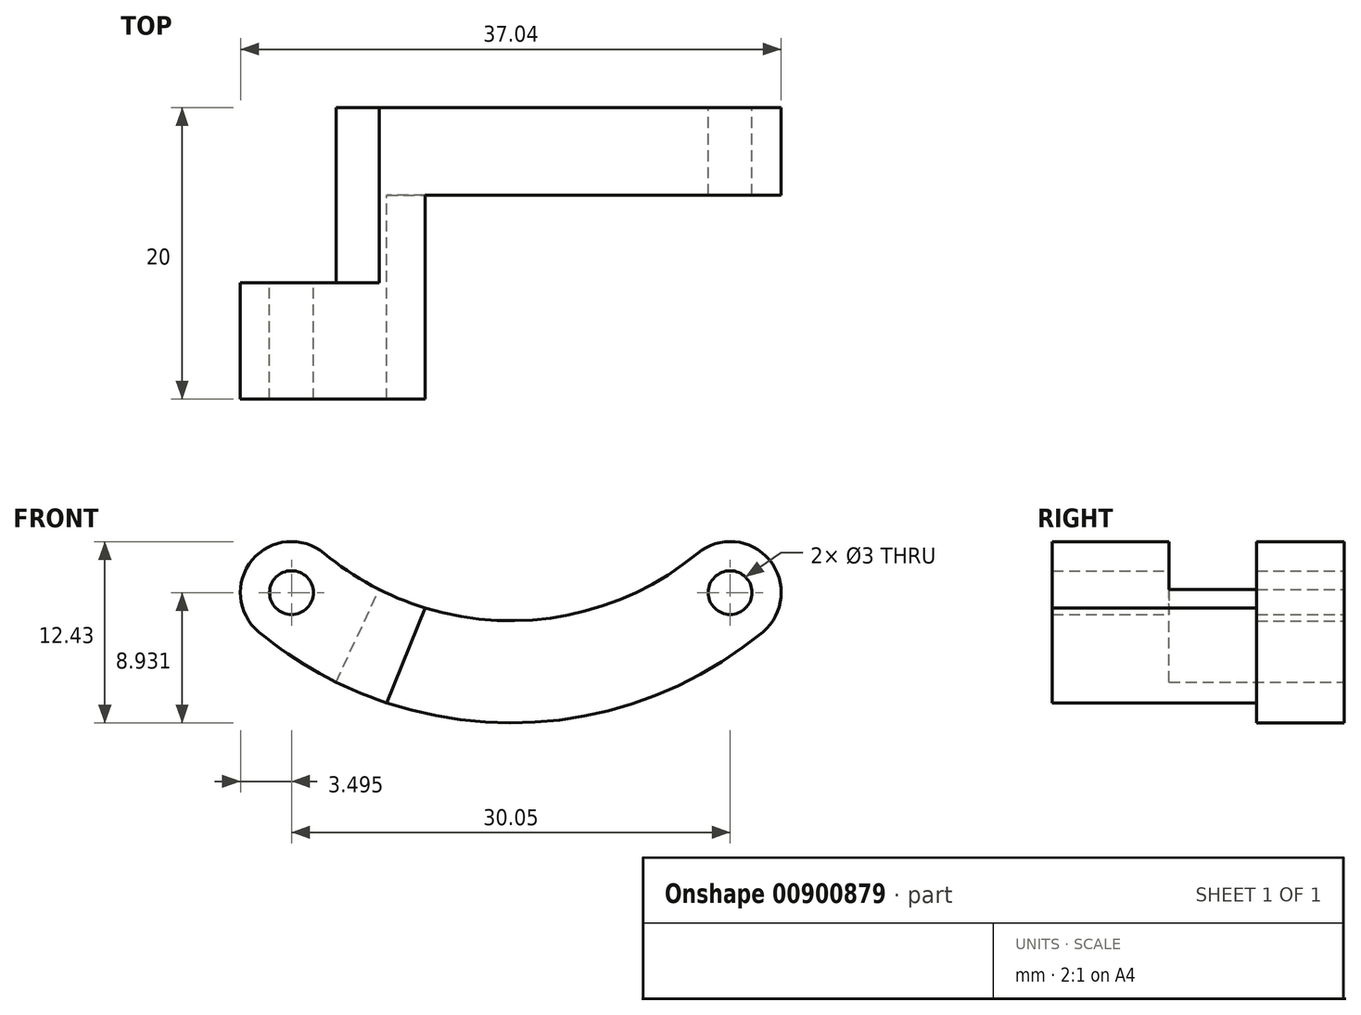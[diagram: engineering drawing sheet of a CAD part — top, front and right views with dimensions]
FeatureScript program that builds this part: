
annotation { "Feature Type Name" : "Feature", "Feature Type Description" : "" }
export const myFeature = defineFeature(function(context is Context, id is Id, definition is map)
    precondition{}
    {
        {
            var Q0;
            Q0=qCreatedBy(makeId("Front.planeOp"),FACE);
            var sketch = newSketch(context, id + "F0", { "sketchPlane" : qUnion([Q0])});
            skArc(sketch, "E0", {"start": v(-12.79, -15.38) * mm, "mid": v(0, -20) * mm, "end": v(12.79, -15.38) * mm});
            skArc(sketch, "E1", {"start": v(-15.02, -18.07) * mm, "mid": v(0, -23.5) * mm, "end": v(15.03, -18.07) * mm});
            skArc(sketch, "E2", {"start": v(-17.26, -20.76) * mm, "mid": v(0, -27) * mm, "end": v(17.26, -20.76) * mm});
            skArc(sketch, "E3", {"start": v(-12.79, -15.38) * mm, "mid": v(-17.72, -15.83) * mm, "end": v(-17.26, -20.76) * mm});
            skArc(sketch, "E4", {"start": v(17.26, -20.76) * mm, "mid": v(17.72, -15.83) * mm, "end": v(12.79, -15.38) * mm});
            skCircle(sketch, "E5", {"center": v(-15.02, -18.07) * mm, "radius": 1.5 * mm});
            skCircle(sketch, "E6", {"center": v(15.03, -18.07) * mm, "radius": 1.5 * mm});
            skSolve(sketch);
        }
        {
            var Q0;
            Q0=makeQuery(id+"F0.imprint","IMPRINT",FACE,{"disambiguationData":[TD([[makeQuery(id+"F0.imprint","IMPRINT",EDGE,{"derivedFrom":sQuery(id+"F0.wireOp",EDGE,"E0")}),-1.0]])]});
            extrude(context, id + "F1", {"entities" : qUnion([Q0]), "endBound" : BoundingType.SYMMETRIC, "depth" : 20 * mm, "offsetDistance" : 25 * mm});
        }
        {
            var Q0;
            Q0=makeQuery(id+"F1.opExtrude","CAP_FACE",FACE,{"disambiguationData":[OSD([sQuery(id+"F0.wireOp",EDGE,"E0"),sQuery(id+"F0.wireOp",EDGE,"E2"),sQuery(id+"F0.wireOp",EDGE,"E3"),sQuery(id+"F0.wireOp",EDGE,"E4"),sQuery(id+"F0.wireOp",EDGE,"E5"),sQuery(id+"F0.wireOp",EDGE,"E6")])],"isStart":false});
            var sketch = newSketch(context, id + "F2", { "sketchPlane" : qUnion([Q0])});
            skLineSegment(sketch, "E7", {"start": v(-3.39, -12.99) * mm, "end": v(-10.21, -29.86) * mm});
            skLineSegment(sketch, "E8", {"start": v(-10.21, -29.86) * mm, "end": v(28.23, -31.5) * mm});
            skLineSegment(sketch, "E9", {"start": v(28.23, -31.5) * mm, "end": v(31.76, -10.08) * mm});
            skLineSegment(sketch, "E10", {"start": v(31.76, -10.08) * mm, "end": v(-3.39, -12.99) * mm});
            skSolve(sketch);
        }
        {
            var Q0;
            {var subQ0=sQuery(id+"F2.wireOp",EDGE,"E8");Q0=makeQuery(id+"F2.imprint","IMPRINT",FACE,{"disambiguationData":[TD([[makeQuery(id+"F2.imprint","IMPRINT",EDGE,{"derivedFrom":subQ0}),1.0]])]});}
            var Q1;
            {var subQ0=makeQuery(id+"F1.opExtrude","CAP_EDGE",EDGE,{"disambiguationData":[OSD([sQuery(id+"F0.wireOp",EDGE,"E4")])],"isStart":false});Q1=makeQuery(id+"F2.imprint","IMPRINT",FACE,{"disambiguationData":[TD([[makeQuery(id+"F2.imprint","IMPRINT",EDGE,{"derivedFrom":subQ0}),1.0]])]});}
            extrude(context, id + "F3", {"entities" : qUnion([Q0, Q1]), "operationType" : NewBodyOperationType.REMOVE, "oppositeDirection" : true, "depth" : 14 * mm, "offsetDistance" : 25 * mm});
        }
        {
            var Q0;
            Q0=makeQuery(id+"F1.opExtrude","CAP_FACE",FACE,{"disambiguationData":[OSD([sQuery(id+"F0.wireOp",EDGE,"E0"),sQuery(id+"F0.wireOp",EDGE,"E2"),sQuery(id+"F0.wireOp",EDGE,"E3"),sQuery(id+"F0.wireOp",EDGE,"E4"),sQuery(id+"F0.wireOp",EDGE,"E5"),sQuery(id+"F0.wireOp",EDGE,"E6")])],"isStart":true});
            var sketch = newSketch(context, id + "F4", { "sketchPlane" : qUnion([Q0])});
            skLineSegment(sketch, "E11", {"start": v(13.55, -27.56) * mm, "end": v(7.36, -14.34) * mm});
            skLineSegment(sketch, "E12", {"start": v(7.36, -14.34) * mm, "end": v(28.16, -12.95) * mm});
            skLineSegment(sketch, "E13", {"start": v(28.16, -12.95) * mm, "end": v(13.55, -27.56) * mm});
            skSolve(sketch);
        }
        {
            var Q0;
            Q0 = qSketchRegion(id + "F4", true);
            extrude(context, id + "F5", {"entities" : qUnion([Q0]), "operationType" : NewBodyOperationType.REMOVE, "oppositeDirection" : true, "depth" : 12 * mm, "offsetDistance" : 25 * mm});
        }
    });
